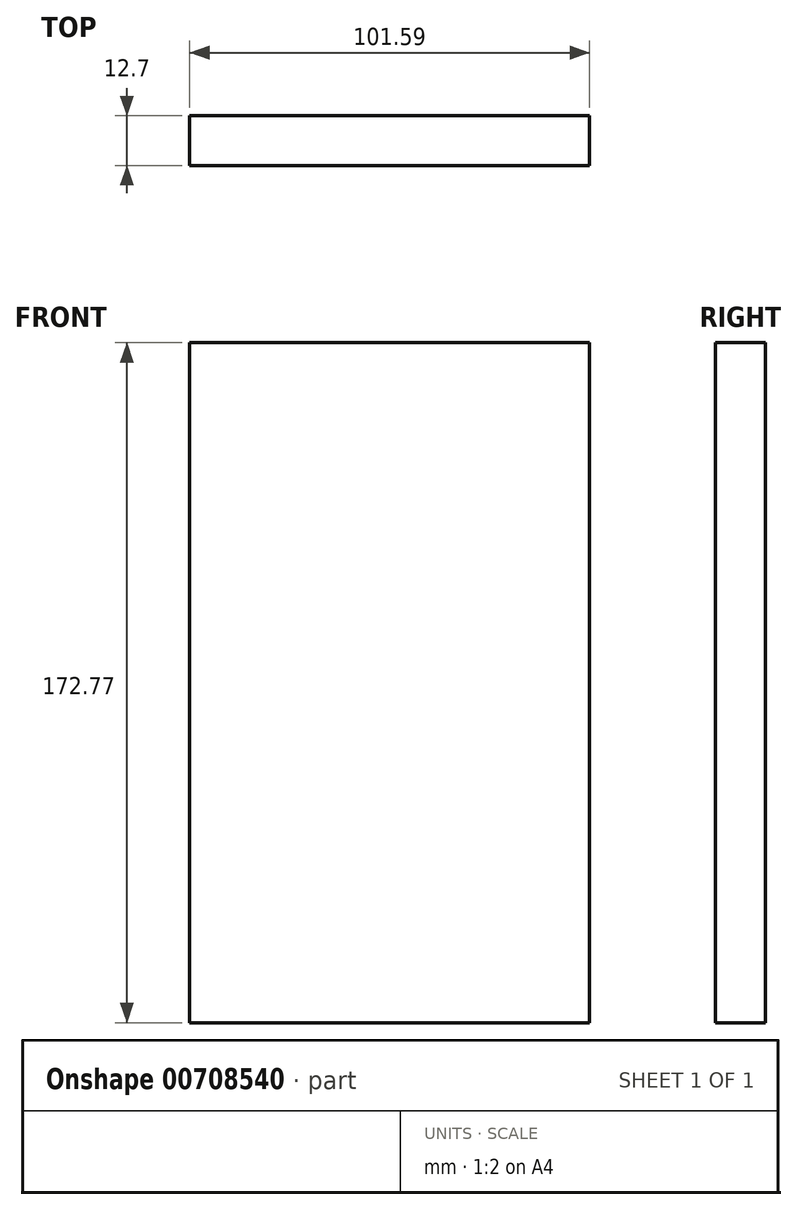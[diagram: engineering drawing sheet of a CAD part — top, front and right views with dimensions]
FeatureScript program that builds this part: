
annotation { "Feature Type Name" : "Feature", "Feature Type Description" : "" }
export const myFeature = defineFeature(function(context is Context, id is Id, definition is map)
    precondition{}
    {
        {
            var Q0;
            Q0=qCreatedBy(makeId("Front.planeOp"),FACE);
            var sketch = newSketch(context, id + "F0", { "sketchPlane" : qUnion([Q0])});
            skLineSegment(sketch, "E0.bottom", {"start": v(-65.27, 79.2) * mm, "end": v(36.32, 79.2) * mm});
            skLineSegment(sketch, "E0.top", {"start": v(-65.27, -93.57) * mm, "end": v(36.32, -93.57) * mm});
            skLineSegment(sketch, "E0.left", {"start": v(-65.27, 79.2) * mm, "end": v(-65.27, -93.57) * mm});
            skLineSegment(sketch, "E0.right", {"start": v(36.32, 79.2) * mm, "end": v(36.32, -93.57) * mm});
            skSolve(sketch);
        }
        {
            var Q0;
            Q0=makeQuery(id+"F0.imprint","IMPRINT",FACE,{"disambiguationData":[TD([[makeQuery(id+"F0.imprint","IMPRINT",EDGE,{"derivedFrom":sQuery(id+"F0.wireOp",EDGE,"E0.bottom")}),-1.0]])]});
            extrude(context, id + "F1", {"entities" : qUnion([Q0]), "depth" : 12.7 * mm, "offsetDistance" : 25.4 * mm});
        }
    });
